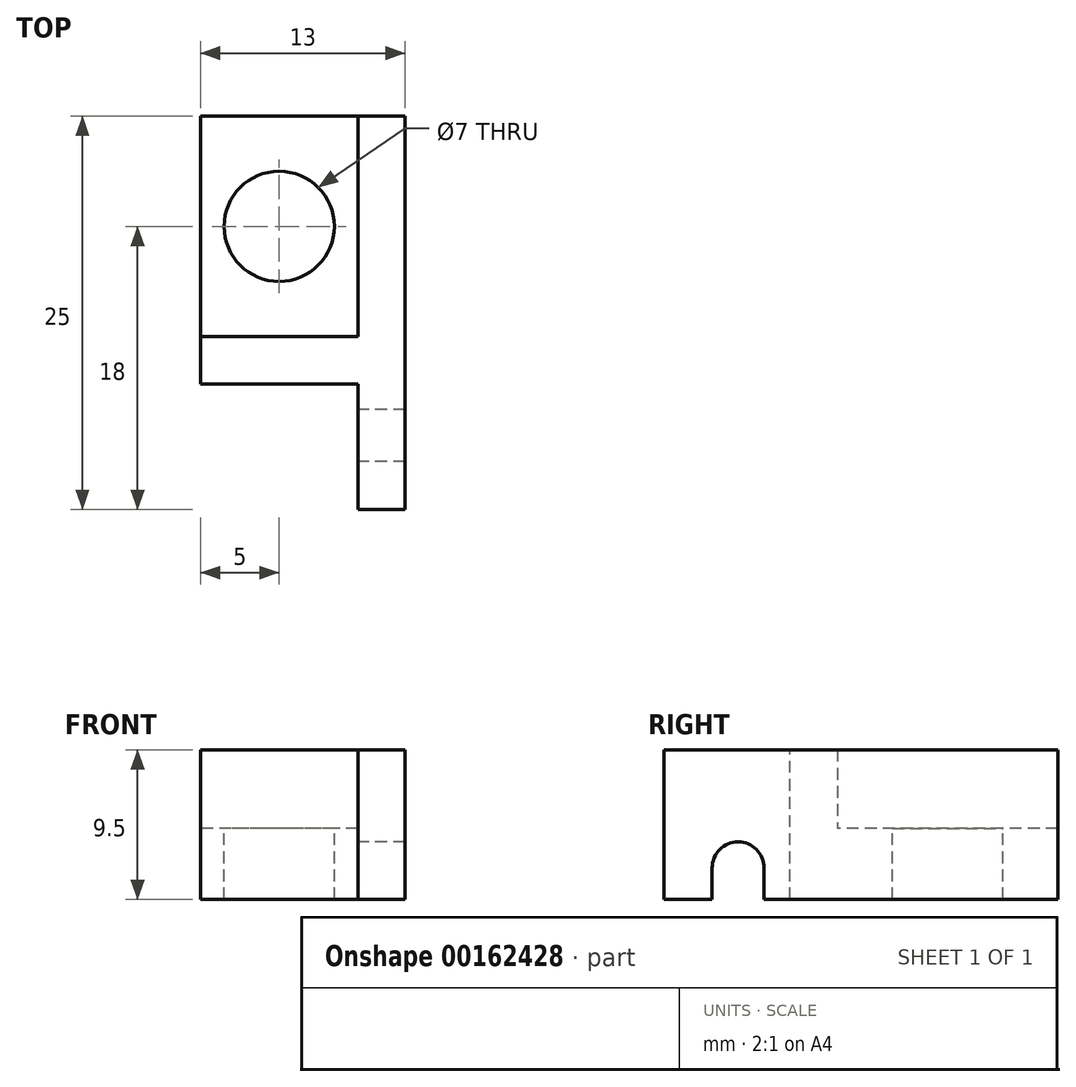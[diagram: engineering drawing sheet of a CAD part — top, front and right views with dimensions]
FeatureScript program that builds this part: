
annotation { "Feature Type Name" : "Feature", "Feature Type Description" : "" }
export const myFeature = defineFeature(function(context is Context, id is Id, definition is map)
    precondition{}
    {
        {
            var Q0;
            Q0=qCreatedBy(makeId("Top.planeOp"),FACE);
            var sketch = newSketch(context, id + "F0", { "sketchPlane" : qUnion([Q0])});
            skLineSegment(sketch, "E0.bottom", {"start": v(5, 7) * mm, "end": v(-5, 7) * mm});
            skLineSegment(sketch, "E0.top", {"start": v(5, -7) * mm, "end": v(-5, -7) * mm});
            skLineSegment(sketch, "E0.left", {"start": v(5, 7) * mm, "end": v(5, -7) * mm});
            skLineSegment(sketch, "E0.right", {"start": v(-5, 7) * mm, "end": v(-5, -7) * mm});
            skPoint(sketch, "E0.middle", {"position": v(0, 0) * mm});
            skCircle(sketch, "E1", {"center": v(0, 0) * mm, "radius": 3.5 * mm});
            skLineSegment(sketch, "E2", {"start": v(-5, -7) * mm, "end": v(-5, -18) * mm});
            skLineSegment(sketch, "E3", {"start": v(-5, -18) * mm, "end": v(8, -18) * mm});
            skLineSegment(sketch, "E4", {"start": v(8, -18) * mm, "end": v(8, 7) * mm});
            skLineSegment(sketch, "E5", {"start": v(8, 7) * mm, "end": v(5, 7) * mm});
            skLineSegment(sketch, "E6", {"start": v(-5, -10) * mm, "end": v(5, -10) * mm});
            skLineSegment(sketch, "E7", {"start": v(5, -10) * mm, "end": v(5, -18) * mm});
            skSolve(sketch);
        }
        {
            var Q0;
            {var subQ4=sQuery(id+"F0.wireOp",EDGE,"E0.top");Q0=makeQuery(id+"F0.imprint","IMPRINT",FACE,{"disambiguationData":[TD([[makeQuery(id+"F0.imprint","IMPRINT",EDGE,{"derivedFrom":subQ4}),1.0]])]});}
            var Q1;
            Q1=makeQuery(id+"F0.imprint","IMPRINT",FACE,{"disambiguationData":[TD([[makeQuery(id+"F0.imprint","IMPRINT",EDGE,{"derivedFrom":sQuery(id+"F0.wireOp",EDGE,"E0.bottom")}),1.0]])]});
            extrude(context, id + "F1", {"entities" : qUnion([Q0, Q1]), "oppositeDirection" : true, "depth" : 4.5 * mm, "offsetDistance" : 25 * mm});
        }
        {
            var Q0;
            {var subQ4=sQuery(id+"F0.wireOp",EDGE,"E0.top");Q0=makeQuery(id+"F0.imprint","IMPRINT",FACE,{"disambiguationData":[TD([[makeQuery(id+"F0.imprint","IMPRINT",EDGE,{"derivedFrom":subQ4}),1.0]])]});}
            extrude(context, id + "F2", {"entities" : qUnion([Q0]), "operationType" : NewBodyOperationType.ADD, "depth" : 5 * mm, "offsetDistance" : 25 * mm});
        }
        {
            var Q0;
            Q0=makeQuery(id+"F2.opExtrude","SWEPT_FACE",FACE,{"disambiguationData":[OSD([sQuery(id+"F0.wireOp",EDGE,"E7")])]});
            var sketch = newSketch(context, id + "F3", { "sketchPlane" : qUnion([Q0])});
            skCircle(sketch, "E8", {"center": v(13.3, -2.5) * mm, "radius": 1.65 * mm});
            skPoint(sketch, "E8.centerSnap1", {"position": v(18, 0.25) * mm});
            skLineSegment(sketch, "E9", {"start": v(11.65, -2.5) * mm, "end": v(11.65, -4.5) * mm});
            skLineSegment(sketch, "E10", {"start": v(14.95, -2.5) * mm, "end": v(14.95, -4.5) * mm});
            skSolve(sketch);
        }
        {
            var Q0;
            {var subQ0=sQuery(id+"F3.wireOp",EDGE,"E9");Q0=makeQuery(id+"F3.imprint","IMPRINT",FACE,{"disambiguationData":[TD([[makeQuery(id+"F3.imprint","IMPRINT",EDGE,{"derivedFrom":subQ0}),1.0]])]});}
            var Q1;
            {var subQ0=sQuery(id+"F3.wireOp",EDGE,"E8");var subQ1=makeQuery(id+"F3.imprint","INTERSECT",VERTEX,{"derivedFrom":[subQ0,sQuery(id+"F3.wireOp",EDGE,"E9")]});Q1=makeQuery(id+"F3.imprint","IMPRINT",FACE,{"disambiguationData":[TD([[makeQuery(id+"F3.imprint","IMPRINT",EDGE,{"disambiguationData":[TD([[subQ1,1.0]])],"derivedFrom":subQ0}),1.0]])]});}
            extrude(context, id + "F4", {"entities" : qUnion([Q0, Q1]), "operationType" : NewBodyOperationType.REMOVE, "oppositeDirection" : true, "depth" : 25 * mm, "offsetDistance" : 25 * mm});
        }
    });
